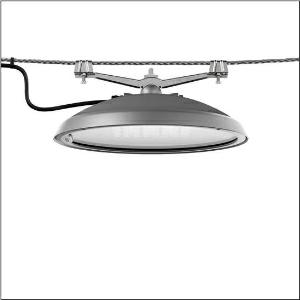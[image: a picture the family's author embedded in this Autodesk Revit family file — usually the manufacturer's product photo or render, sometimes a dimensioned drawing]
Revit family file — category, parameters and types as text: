
# Revit family: dl_50_iq_mini___st1_0s_5xa248w21f08he_1368
name_source: partatom
category: Lighting Fixtures
units: mm (PartAtom-declared; Revit-internal decimal feet)

## family parameters
Cut with Voids When Loaded = No
Host = Face
Light Source = No
Part Type = Normal
Room Calculation Point = No
Round Connector Dimension = Use Diameter
Shared = No

## types (1)
- --- (1 x LED, 7840 lm, 69.3 W, 2200K)
    Apparent Load = 69 VA
    CIE Flux Codes = 37 72 97 100 100
    Color Rendering = 70
    Color Temperature = 2200K
    Default Elevation = 1800 mm
    Description = DL 50 iQ mini, catenary luminaire, primary light control with lens, of PMMA, primary optical cover: cover, of toughened safety glass, transparent, light distribution: ST1.0s, light emission: direct distribution, primary light characteristic: symmetric, installation type: suspended mounting, LED, High Power LED, rated luminous flux: 7.840lm, luminous efficacy: 113lm/W, light colour: 722, colour temperature: 2200K, control gear: iQ Street-Remote, control: optimised constant luminous flux control (CLO 2.0), Desk-Remote (wireless, voltage-free reading and setting of iQ features in the workshop via application-optimized NFC function/RFID function), Light-Fading, Smart-Wire, Night-Set, Lumen-Switch, Temp-Guard, Auto-Match, Street-Remote, mains connection: 230..240V, AC, 50/60Hz, start of lifetime: 69W, end of service life: 74W, reduction: 30W, luminaire housing, of diecast aluminium, powder-coated, SITECO metallic grey (DB 702S), diameter: 500mm, height: 115mm, mounting height: 4..12m, protection rating (complete): IP66, insulation class (complete): insulation class II (safety insulation), certification: CE, ENEC, ENEC+, VDE, impact resistance: IK08, permissible operating ambient temperature for outdoor applications: -25..+40°C, standard-compliant lighting for roads and squares, packaging unit: 1 piece

Light Distribution: ST1.0s
    Height = 124 mm  [stored 0.406824 ft]
    Lamp = 1 x LED
    Lamp Light Flux = 7840 lm
    Lamp Power = 69.3 W
    Lamp count = 1
    Length = 500 mm
    Luminous efficacy = 113 lm/W
    Manufacturer = Siteco
    ModVariant = No
    Model = 5XA248W21F08HE
    Number of Poles = 1
    OnlyDefault = Yes
    Power Factor = 1
    Product Name = DL 50 iQ mini | ST1.0s
    Product group = catenary luminaire
    ProductGroupID = 6300
    Protection Class = Protection class II
    Protection Degree = IP 66
    RLX_Detail_Level = 1
    RLX_Emergency_Light_Flux = 0 lm
    RLX_Emergency_Type = 0
    RLX_Emergency_Type_DB = No
    RlxData = <blob elided: 123657 chars, md5=e28a43e5>
    Socket = socket
    Standby Power = 0 W
    System Light Flux = 7840 lm
    System Power = 69 W
    Type Comments = factory setting: luminous flux: 100 % | dim-lin: 254 | 700 mA
    Type Image = l_1242791.jpg
    URL = http://relux.com
    VarID = @adj_141729
    Voltage = 0 V
    Weight = 0.00 kg
    Width = 0 mm  [stored 0 ft]

note: [stored X ft] marks values corroborated as IEEE doubles in the binary element streams (Revit-internal decimal feet)

## geometry (parser evidence)
native form markers: Blend x4, Sweep x12
no freeform markers — native parametric forms only
